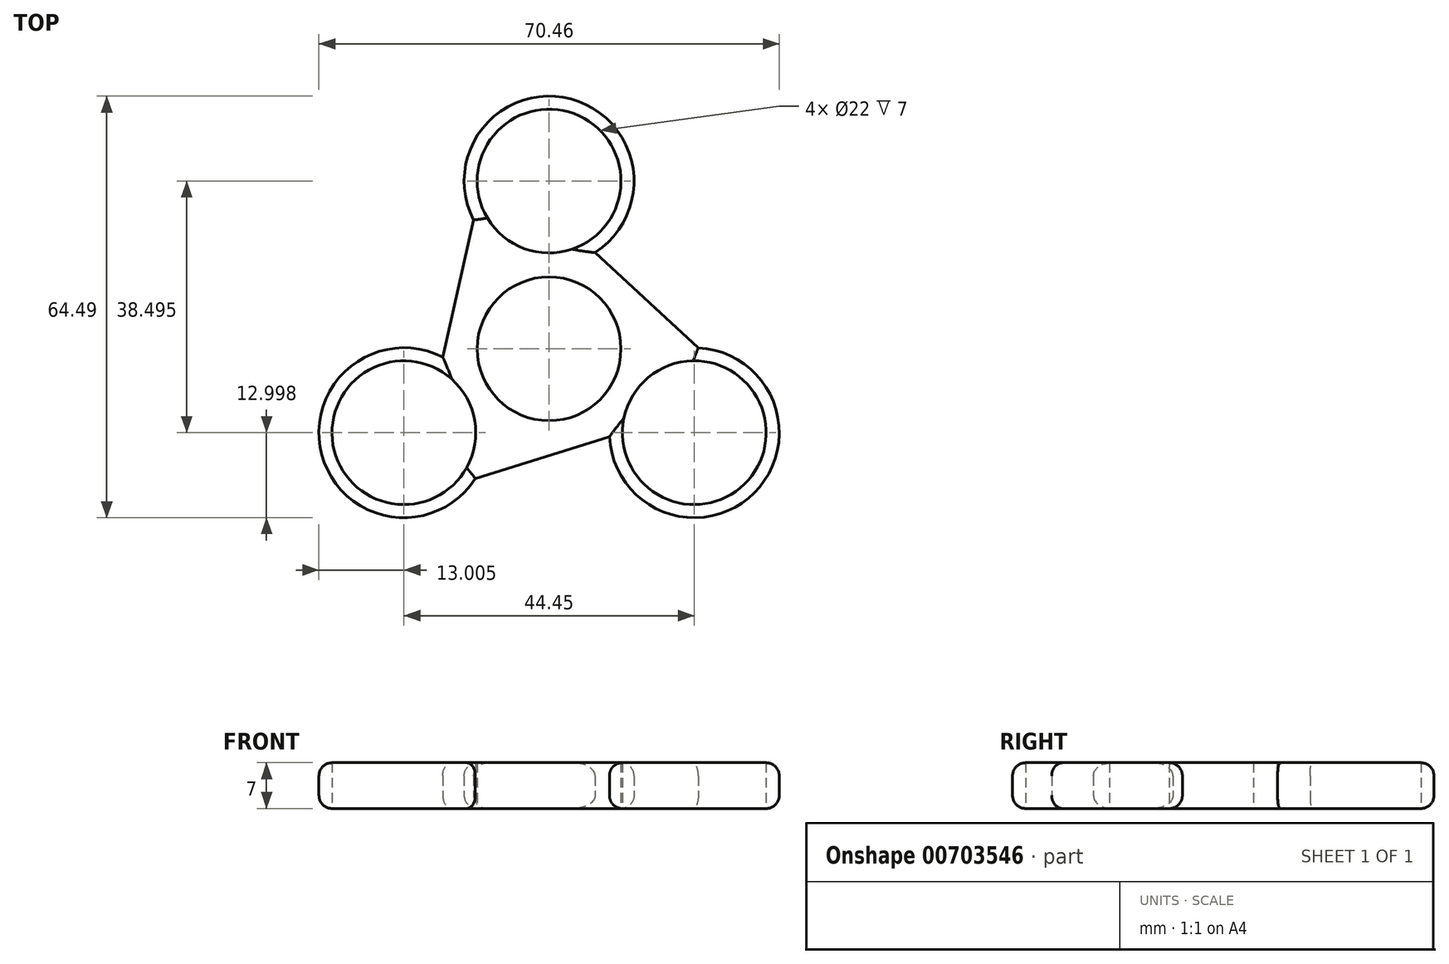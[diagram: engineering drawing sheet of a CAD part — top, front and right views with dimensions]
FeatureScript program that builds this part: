
annotation { "Feature Type Name" : "Feature", "Feature Type Description" : "" }
export const myFeature = defineFeature(function(context is Context, id is Id, definition is map)
    precondition{}
    {
        {
            var Q0;
            Q0=qCreatedBy(makeId("Top.planeOp"),FACE);
            var sketch = newSketch(context, id + "F0", { "sketchPlane" : qUnion([Q0])});
            skCircle(sketch, "E0", {"center": v(0, 0) * mm, "radius": 11 * mm});
            skCircle(sketch, "E1", {"center": v(0, 0) * mm, "radius": 25.66 * mm});
            skLineSegment(sketch, "E2", {"start": v(0, 0) * mm, "end": v(0, 25.66) * mm});
            skLineSegment(sketch, "E3", {"start": v(0, 0) * mm, "end": v(-22.23, -12.83) * mm});
            skLineSegment(sketch, "E4", {"start": v(0, 0) * mm, "end": v(22.22, -12.83) * mm});
            skLineSegment(sketch, "E5", {"start": v(-22.23, -12.83) * mm, "end": v(22.22, -12.83) * mm});
            skLineSegment(sketch, "E6", {"start": v(0, 25.66) * mm, "end": v(22.22, -12.83) * mm});
            skLineSegment(sketch, "E7", {"start": v(0, 25.66) * mm, "end": v(-22.23, -12.83) * mm});
            skCircle(sketch, "E8", {"center": v(0, 25.66) * mm, "radius": 11 * mm});
            skCircle(sketch, "E9", {"center": v(22.22, -12.83) * mm, "radius": 11 * mm});
            skCircle(sketch, "E10", {"center": v(-22.23, -12.83) * mm, "radius": 11 * mm});
            skLineSegment(sketch, "E11", {"start": v(-10.74, 23.3) * mm, "end": v(-16.73, -3.3) * mm});
            skLineSegment(sketch, "E12", {"start": v(10.74, 23.3) * mm, "end": v(0, 0) * mm});
            skLineSegment(sketch, "E13", {"start": v(-25.56, -2.35) * mm, "end": v(0, 0) * mm});
            skLineSegment(sketch, "E14", {"start": v(14.81, -20.96) * mm, "end": v(0, 0) * mm});
            skCircle(sketch, "E15", {"center": v(-22.23, -12.83) * mm, "radius": 13 * mm});
            skCircle(sketch, "E16", {"center": v(22.22, -12.83) * mm, "radius": 13 * mm});
            skCircle(sketch, "E17", {"center": v(0, 25.66) * mm, "radius": 13 * mm});
            skLineSegment(sketch, "E18", {"start": v(-72.04, -0.14) * mm, "end": v(-63.63, 27.97) * mm});
            skLineSegment(sketch, "E19", {"start": v(25.56, -2.35) * mm, "end": v(5.5, 16.14) * mm});
            skLineSegment(sketch, "E20", {"start": v(-14.81, -20.96) * mm, "end": v(11.22, -12.83) * mm});
            skSolve(sketch);
        }
        {
            var Q0;
            {var subQ1=sQuery(id+"F0.wireOp",EDGE,"E0");var subQ7=sQuery(id+"F0.wireOp",EDGE,"E2");var subQ8=makeQuery(id+"F0.imprint","INTERSECT",VERTEX,{"derivedFrom":[subQ1,subQ7]});Q0=makeQuery(id+"F0.imprint","IMPRINT",FACE,{"disambiguationData":[TD([[makeQuery(id+"F0.imprint","IMPRINT",EDGE,{"disambiguationData":[TD([[subQ8,-1.0]])],"derivedFrom":subQ1}),-1.0]])]});}
            var Q1;
            {var subQ0=sQuery(id+"F0.wireOp",EDGE,"E12");var subQ1=sQuery(id+"F0.wireOp",EDGE,"E0");var subQ2=makeQuery(id+"F0.imprint","INTERSECT",VERTEX,{"derivedFrom":[subQ1,subQ0]});Q1=makeQuery(id+"F0.imprint","IMPRINT",FACE,{"disambiguationData":[TD([[makeQuery(id+"F0.imprint","IMPRINT",EDGE,{"disambiguationData":[TD([[subQ2,1.0]])],"derivedFrom":subQ1}),-1.0]])]});}
            var Q2;
            {var subQ1=sQuery(id+"F0.wireOp",EDGE,"E0");var subQ7=sQuery(id+"F0.wireOp",EDGE,"E3");var subQ8=makeQuery(id+"F0.imprint","INTERSECT",VERTEX,{"derivedFrom":[subQ1,subQ7]});Q2=makeQuery(id+"F0.imprint","IMPRINT",FACE,{"disambiguationData":[TD([[makeQuery(id+"F0.imprint","IMPRINT",EDGE,{"disambiguationData":[TD([[subQ8,-1.0]])],"derivedFrom":subQ1}),-1.0]])]});}
            var Q3;
            {var subQ0=sQuery(id+"F0.wireOp",EDGE,"E13");var subQ1=sQuery(id+"F0.wireOp",EDGE,"E0");var subQ2=makeQuery(id+"F0.imprint","INTERSECT",VERTEX,{"derivedFrom":[subQ1,subQ0]});Q3=makeQuery(id+"F0.imprint","IMPRINT",FACE,{"disambiguationData":[TD([[makeQuery(id+"F0.imprint","IMPRINT",EDGE,{"disambiguationData":[TD([[subQ2,-1.0]])],"derivedFrom":subQ1}),-1.0]])]});}
            var Q4;
            {var subQ5=sQuery(id+"F0.wireOp",EDGE,"E0");var subQ7=sQuery(id+"F0.wireOp",EDGE,"E2");var subQ8=makeQuery(id+"F0.imprint","INTERSECT",VERTEX,{"derivedFrom":[subQ5,subQ7]});Q4=makeQuery(id+"F0.imprint","IMPRINT",FACE,{"disambiguationData":[TD([[makeQuery(id+"F0.imprint","IMPRINT",EDGE,{"disambiguationData":[TD([[subQ8,1.0]])],"derivedFrom":subQ5}),-1.0]])]});}
            var Q5;
            {var subQ0=sQuery(id+"F0.wireOp",EDGE,"E14");var subQ7=sQuery(id+"F0.wireOp",EDGE,"E0");var subQ9=makeQuery(id+"F0.imprint","INTERSECT",VERTEX,{"derivedFrom":[subQ7,subQ0]});Q5=makeQuery(id+"F0.imprint","IMPRINT",FACE,{"disambiguationData":[TD([[makeQuery(id+"F0.imprint","IMPRINT",EDGE,{"disambiguationData":[TD([[subQ9,-1.0]])],"derivedFrom":subQ7}),-1.0]])]});}
            var Q6;
            {var subQ5=sQuery(id+"F0.wireOp",EDGE,"E15");var subQ6=sQuery(id+"F0.wireOp",EDGE,"E5");var subQ7=makeQuery(id+"F0.imprint","INTERSECT",VERTEX,{"derivedFrom":[subQ6,subQ5]});Q6=makeQuery(id+"F0.imprint","IMPRINT",FACE,{"disambiguationData":[TD([[makeQuery(id+"F0.imprint","IMPRINT",EDGE,{"disambiguationData":[TD([[subQ7,-1.0]])],"derivedFrom":subQ6}),-1.0]])]});}
            var Q7;
            {var subQ1=sQuery(id+"F0.wireOp",EDGE,"E6");var subQ5=sQuery(id+"F0.wireOp",EDGE,"E12");var subQ6=makeQuery(id+"F0.imprint","INTERSECT",VERTEX,{"derivedFrom":[subQ1,subQ5]});Q7=makeQuery(id+"F0.imprint","IMPRINT",FACE,{"disambiguationData":[TD([[makeQuery(id+"F0.imprint","IMPRINT",EDGE,{"disambiguationData":[TD([[subQ6,-1.0]])],"derivedFrom":subQ1}),1.0]])]});}
            var Q8;
            {var subQ5=sQuery(id+"F0.wireOp",EDGE,"E17");var subQ7=sQuery(id+"F0.wireOp",EDGE,"E7");var subQ9=makeQuery(id+"F0.imprint","INTERSECT",VERTEX,{"derivedFrom":[subQ7,subQ5]});Q8=makeQuery(id+"F0.imprint","IMPRINT",FACE,{"disambiguationData":[TD([[makeQuery(id+"F0.imprint","IMPRINT",EDGE,{"disambiguationData":[TD([[subQ9,-1.0]])],"derivedFrom":subQ7}),-1.0]])]});}
            var Q9;
            {var subQ0=sQuery(id+"F0.wireOp",EDGE,"E8");var subQ1=sQuery(id+"F0.wireOp",EDGE,"E7");var subQ2=makeQuery(id+"F0.imprint","INTERSECT",VERTEX,{"derivedFrom":[subQ1,subQ0]});Q9=makeQuery(id+"F0.imprint","IMPRINT",FACE,{"disambiguationData":[TD([[makeQuery(id+"F0.imprint","IMPRINT",EDGE,{"disambiguationData":[TD([[subQ2,-1.0]])],"derivedFrom":subQ1}),-1.0]])]});}
            var Q10;
            {var subQ1=sQuery(id+"F0.wireOp",EDGE,"E1");var subQ3=sQuery(id+"F0.wireOp",EDGE,"E17");var subQ4=makeQuery(id+"F0.imprint","INTERSECT",VERTEX,{"disambiguationData":[OD(1.0)],"derivedFrom":[subQ1,subQ3]});Q10=makeQuery(id+"F0.imprint","IMPRINT",FACE,{"disambiguationData":[TD([[makeQuery(id+"F0.imprint","IMPRINT",EDGE,{"disambiguationData":[TD([[subQ4,-1.0]])],"derivedFrom":subQ3}),1.0]])]});}
            var Q11;
            {var subQ1=sQuery(id+"F0.wireOp",EDGE,"E1");var subQ3=sQuery(id+"F0.wireOp",EDGE,"E17");var subQ4=makeQuery(id+"F0.imprint","INTERSECT",VERTEX,{"disambiguationData":[OD(0.0)],"derivedFrom":[subQ1,subQ3]});Q11=makeQuery(id+"F0.imprint","IMPRINT",FACE,{"disambiguationData":[TD([[makeQuery(id+"F0.imprint","IMPRINT",EDGE,{"disambiguationData":[TD([[subQ4,-1.0]])],"derivedFrom":subQ3}),1.0]])]});}
            var Q12;
            {var subQ0=sQuery(id+"F0.wireOp",EDGE,"E16");var subQ1=sQuery(id+"F0.wireOp",EDGE,"E6");var subQ2=makeQuery(id+"F0.imprint","INTERSECT",VERTEX,{"derivedFrom":[subQ1,subQ0]});Q12=makeQuery(id+"F0.imprint","IMPRINT",FACE,{"disambiguationData":[TD([[makeQuery(id+"F0.imprint","IMPRINT",EDGE,{"disambiguationData":[TD([[subQ2,-1.0]])],"derivedFrom":subQ1}),1.0]])]});}
            var Q13;
            {var subQ1=sQuery(id+"F0.wireOp",EDGE,"E1");var subQ3=sQuery(id+"F0.wireOp",EDGE,"E16");var subQ4=makeQuery(id+"F0.imprint","INTERSECT",VERTEX,{"disambiguationData":[OD(1.0)],"derivedFrom":[subQ1,subQ3]});Q13=makeQuery(id+"F0.imprint","IMPRINT",FACE,{"disambiguationData":[TD([[makeQuery(id+"F0.imprint","IMPRINT",EDGE,{"disambiguationData":[TD([[subQ4,-1.0]])],"derivedFrom":subQ3}),1.0]])]});}
            var Q14;
            {var subQ1=sQuery(id+"F0.wireOp",EDGE,"E1");var subQ3=sQuery(id+"F0.wireOp",EDGE,"E16");var subQ4=makeQuery(id+"F0.imprint","INTERSECT",VERTEX,{"disambiguationData":[OD(0.0)],"derivedFrom":[subQ1,subQ3]});Q14=makeQuery(id+"F0.imprint","IMPRINT",FACE,{"disambiguationData":[TD([[makeQuery(id+"F0.imprint","IMPRINT",EDGE,{"disambiguationData":[TD([[subQ4,-1.0]])],"derivedFrom":subQ3}),1.0]])]});}
            var Q15;
            {var subQ0=sQuery(id+"F0.wireOp",EDGE,"E16");var subQ1=sQuery(id+"F0.wireOp",EDGE,"E4");var subQ2=makeQuery(id+"F0.imprint","INTERSECT",VERTEX,{"derivedFrom":[subQ1,subQ0]});Q15=makeQuery(id+"F0.imprint","IMPRINT",FACE,{"disambiguationData":[TD([[makeQuery(id+"F0.imprint","IMPRINT",EDGE,{"disambiguationData":[TD([[subQ2,-1.0]])],"derivedFrom":subQ1}),1.0]])]});}
            var Q16;
            {var subQ0=sQuery(id+"F0.wireOp",EDGE,"E16");var subQ1=sQuery(id+"F0.wireOp",EDGE,"E4");var subQ2=makeQuery(id+"F0.imprint","INTERSECT",VERTEX,{"derivedFrom":[subQ1,subQ0]});Q16=makeQuery(id+"F0.imprint","IMPRINT",FACE,{"disambiguationData":[TD([[makeQuery(id+"F0.imprint","IMPRINT",EDGE,{"disambiguationData":[TD([[subQ2,-1.0]])],"derivedFrom":subQ1}),-1.0]])]});}
            var Q17;
            {var subQ0=sQuery(id+"F0.wireOp",EDGE,"E15");var subQ1=sQuery(id+"F0.wireOp",EDGE,"E3");var subQ2=makeQuery(id+"F0.imprint","INTERSECT",VERTEX,{"derivedFrom":[subQ1,subQ0]});Q17=makeQuery(id+"F0.imprint","IMPRINT",FACE,{"disambiguationData":[TD([[makeQuery(id+"F0.imprint","IMPRINT",EDGE,{"disambiguationData":[TD([[subQ2,-1.0]])],"derivedFrom":subQ1}),1.0]])]});}
            var Q18;
            {var subQ0=sQuery(id+"F0.wireOp",EDGE,"E15");var subQ1=sQuery(id+"F0.wireOp",EDGE,"E3");var subQ2=makeQuery(id+"F0.imprint","INTERSECT",VERTEX,{"derivedFrom":[subQ1,subQ0]});Q18=makeQuery(id+"F0.imprint","IMPRINT",FACE,{"disambiguationData":[TD([[makeQuery(id+"F0.imprint","IMPRINT",EDGE,{"disambiguationData":[TD([[subQ2,-1.0]])],"derivedFrom":subQ1}),-1.0]])]});}
            var Q19;
            {var subQ0=sQuery(id+"F0.wireOp",EDGE,"E17");var subQ1=sQuery(id+"F0.wireOp",EDGE,"E2");var subQ2=makeQuery(id+"F0.imprint","INTERSECT",VERTEX,{"derivedFrom":[subQ1,subQ0]});Q19=makeQuery(id+"F0.imprint","IMPRINT",FACE,{"disambiguationData":[TD([[makeQuery(id+"F0.imprint","IMPRINT",EDGE,{"disambiguationData":[TD([[subQ2,-1.0]])],"derivedFrom":subQ1}),1.0]])]});}
            var Q20;
            {var subQ0=sQuery(id+"F0.wireOp",EDGE,"E17");var subQ1=sQuery(id+"F0.wireOp",EDGE,"E2");var subQ2=makeQuery(id+"F0.imprint","INTERSECT",VERTEX,{"derivedFrom":[subQ1,subQ0]});Q20=makeQuery(id+"F0.imprint","IMPRINT",FACE,{"disambiguationData":[TD([[makeQuery(id+"F0.imprint","IMPRINT",EDGE,{"disambiguationData":[TD([[subQ2,-1.0]])],"derivedFrom":subQ1}),-1.0]])]});}
            extrude(context, id + "F1", {"entities" : qUnion([Q0, Q1, Q2, Q3, Q4, Q5, Q6, Q7, Q8, Q9, Q10, Q11, Q12, Q13, Q14, Q15, Q16, Q17, Q18, Q19, Q20]), "depth" : 7 * mm, "offsetDistance" : 25.4 * mm});
        }
        {
            var Q0;
            {var subQ0=sQuery(id+"F0.wireOp",EDGE,"E10");var subQ1=sQuery(id+"F0.wireOp",EDGE,"E5");var subQ2=makeQuery(id+"F0.imprint","INTERSECT",VERTEX,{"derivedFrom":[subQ1,subQ0]});Q0=makeQuery(id+"F0.imprint","IMPRINT",FACE,{"disambiguationData":[TD([[makeQuery(id+"F0.imprint","IMPRINT",EDGE,{"disambiguationData":[TD([[subQ2,-1.0]])],"derivedFrom":subQ1}),-1.0]])]});}
            var Q1;
            {var subQ1=sQuery(id+"F0.wireOp",EDGE,"E1");var subQ3=sQuery(id+"F0.wireOp",EDGE,"E15");var subQ4=makeQuery(id+"F0.imprint","INTERSECT",VERTEX,{"disambiguationData":[OD(1.0)],"derivedFrom":[subQ1,subQ3]});Q1=makeQuery(id+"F0.imprint","IMPRINT",FACE,{"disambiguationData":[TD([[makeQuery(id+"F0.imprint","IMPRINT",EDGE,{"disambiguationData":[TD([[subQ4,-1.0]])],"derivedFrom":subQ3}),1.0]])]});}
            var Q2;
            {var subQ1=sQuery(id+"F0.wireOp",EDGE,"E9");var subQ3=sQuery(id+"F0.wireOp",EDGE,"E14");var subQ4=makeQuery(id+"F0.imprint","INTERSECT",VERTEX,{"derivedFrom":[subQ1,subQ3]});Q2=makeQuery(id+"F0.imprint","IMPRINT",FACE,{"disambiguationData":[TD([[makeQuery(id+"F0.imprint","IMPRINT",EDGE,{"disambiguationData":[TD([[subQ4,-1.0]])],"derivedFrom":subQ3}),-1.0]])]});}
            extrude(context, id + "F2", {"entities" : qUnion([Q0, Q1, Q2]), "operationType" : NewBodyOperationType.ADD, "depth" : 7 * mm, "offsetDistance" : 25.4 * mm});
        }
        {
            var Q0;
            {var subQ1=sQuery(id+"F0.wireOp",EDGE,"E8");var subQ3=sQuery(id+"F0.wireOp",EDGE,"E12");var subQ4=makeQuery(id+"F0.imprint","INTERSECT",VERTEX,{"derivedFrom":[subQ1,subQ3]});Q0=makeQuery(id+"F0.imprint","IMPRINT",FACE,{"disambiguationData":[TD([[makeQuery(id+"F0.imprint","IMPRINT",EDGE,{"disambiguationData":[TD([[subQ4,-1.0]])],"derivedFrom":subQ3}),-1.0]])]});}
            var Q1;
            {var subQ0=sQuery(id+"F0.wireOp",EDGE,"E20");var subQ5=sQuery(id+"F0.wireOp",EDGE,"E14");var subQ6=makeQuery(id+"F0.imprint","INTERSECT",VERTEX,{"derivedFrom":[subQ5,subQ0]});Q1=makeQuery(id+"F0.imprint","IMPRINT",FACE,{"disambiguationData":[TD([[makeQuery(id+"F0.imprint","IMPRINT",EDGE,{"disambiguationData":[TD([[subQ6,-1.0]])],"derivedFrom":subQ5}),-1.0]])]});}
            var Q2;
            {var subQ0=sQuery(id+"F0.wireOp",EDGE,"E14");var subQ1=sQuery(id+"F0.wireOp",EDGE,"E5");var subQ2=makeQuery(id+"F0.imprint","INTERSECT",VERTEX,{"derivedFrom":[subQ1,subQ0]});Q2=makeQuery(id+"F0.imprint","IMPRINT",FACE,{"disambiguationData":[TD([[makeQuery(id+"F0.imprint","IMPRINT",EDGE,{"disambiguationData":[TD([[subQ2,-1.0]])],"derivedFrom":subQ1}),-1.0]])]});}
            var Q3;
            {var subQ0=sQuery(id+"F0.wireOp",EDGE,"E20");var subQ1=sQuery(id+"F0.wireOp",EDGE,"E14");var subQ2=makeQuery(id+"F0.imprint","INTERSECT",VERTEX,{"derivedFrom":[subQ1,subQ0]});Q3=makeQuery(id+"F0.imprint","IMPRINT",FACE,{"disambiguationData":[TD([[makeQuery(id+"F0.imprint","IMPRINT",EDGE,{"disambiguationData":[TD([[subQ2,-1.0]])],"derivedFrom":subQ1}),1.0]])]});}
            var Q4;
            {var subQ5=sQuery(id+"F0.wireOp",EDGE,"E14");var subQ6=sQuery(id+"F0.wireOp",EDGE,"E9");var subQ8=makeQuery(id+"F0.imprint","INTERSECT",VERTEX,{"derivedFrom":[subQ6,subQ5]});Q4=makeQuery(id+"F0.imprint","IMPRINT",FACE,{"disambiguationData":[TD([[makeQuery(id+"F0.imprint","IMPRINT",EDGE,{"disambiguationData":[TD([[subQ8,-1.0]])],"derivedFrom":subQ5}),1.0]])]});}
            var Q5;
            {var subQ0=sQuery(id+"F0.wireOp",EDGE,"E15");var subQ1=sQuery(id+"F0.wireOp",EDGE,"E11");var subQ2=makeQuery(id+"F0.imprint","INTERSECT",VERTEX,{"derivedFrom":[subQ1,subQ0]});Q5=makeQuery(id+"F0.imprint","IMPRINT",FACE,{"disambiguationData":[TD([[makeQuery(id+"F0.imprint","IMPRINT",EDGE,{"disambiguationData":[TD([[subQ2,-1.0]])],"derivedFrom":subQ1}),1.0]])]});}
            var Q6;
            {var subQ0=sQuery(id+"F0.wireOp",EDGE,"E11");var subQ5=sQuery(id+"F0.wireOp",EDGE,"E13");var subQ6=makeQuery(id+"F0.imprint","INTERSECT",VERTEX,{"derivedFrom":[subQ0,subQ5]});Q6=makeQuery(id+"F0.imprint","IMPRINT",FACE,{"disambiguationData":[TD([[makeQuery(id+"F0.imprint","IMPRINT",EDGE,{"disambiguationData":[TD([[subQ6,-1.0]])],"derivedFrom":subQ5}),-1.0]])]});}
            var Q7;
            {var subQ0=sQuery(id+"F0.wireOp",EDGE,"E13");var subQ1=sQuery(id+"F0.wireOp",EDGE,"E7");var subQ2=makeQuery(id+"F0.imprint","INTERSECT",VERTEX,{"derivedFrom":[subQ1,subQ0]});Q7=makeQuery(id+"F0.imprint","IMPRINT",FACE,{"disambiguationData":[TD([[makeQuery(id+"F0.imprint","IMPRINT",EDGE,{"disambiguationData":[TD([[subQ2,-1.0]])],"derivedFrom":subQ1}),-1.0]])]});}
            var Q8;
            {var subQ0=sQuery(id+"F0.wireOp",EDGE,"E19");var subQ5=sQuery(id+"F0.wireOp",EDGE,"E12");var subQ6=makeQuery(id+"F0.imprint","INTERSECT",VERTEX,{"derivedFrom":[subQ5,subQ0]});Q8=makeQuery(id+"F0.imprint","IMPRINT",FACE,{"disambiguationData":[TD([[makeQuery(id+"F0.imprint","IMPRINT",EDGE,{"disambiguationData":[TD([[subQ6,-1.0]])],"derivedFrom":subQ5}),-1.0]])]});}
            var Q9;
            {var subQ0=sQuery(id+"F0.wireOp",EDGE,"E17");var subQ1=sQuery(id+"F0.wireOp",EDGE,"E6");var subQ2=makeQuery(id+"F0.imprint","INTERSECT",VERTEX,{"derivedFrom":[subQ1,subQ0]});Q9=makeQuery(id+"F0.imprint","IMPRINT",FACE,{"disambiguationData":[TD([[makeQuery(id+"F0.imprint","IMPRINT",EDGE,{"disambiguationData":[TD([[subQ2,-1.0]])],"derivedFrom":subQ1}),1.0]])]});}
            var Q10;
            {var subQ0=sQuery(id+"F0.wireOp",EDGE,"E19");var subQ1=sQuery(id+"F0.wireOp",EDGE,"E12");var subQ2=makeQuery(id+"F0.imprint","INTERSECT",VERTEX,{"derivedFrom":[subQ1,subQ0]});Q10=makeQuery(id+"F0.imprint","IMPRINT",FACE,{"disambiguationData":[TD([[makeQuery(id+"F0.imprint","IMPRINT",EDGE,{"disambiguationData":[TD([[subQ2,-1.0]])],"derivedFrom":subQ1}),1.0]])]});}
            var Q11;
            {var subQ5=sQuery(id+"F0.wireOp",EDGE,"E12");var subQ6=sQuery(id+"F0.wireOp",EDGE,"E8");var subQ7=makeQuery(id+"F0.imprint","INTERSECT",VERTEX,{"derivedFrom":[subQ6,subQ5]});Q11=makeQuery(id+"F0.imprint","IMPRINT",FACE,{"disambiguationData":[TD([[makeQuery(id+"F0.imprint","IMPRINT",EDGE,{"disambiguationData":[TD([[subQ7,-1.0]])],"derivedFrom":subQ5}),1.0]])]});}
            extrude(context, id + "F3", {"entities" : qUnion([Q0, Q1, Q2, Q3, Q4, Q5, Q6, Q7, Q8, Q9, Q10, Q11]), "operationType" : NewBodyOperationType.ADD, "depth" : 7 * mm, "offsetDistance" : 25.4 * mm});
        }
        {
            var Q0;
            {var subQ3=sQuery(id+"F0.wireOp",EDGE,"E11");var subQ5=sQuery(id+"F0.wireOp",EDGE,"E15");var subQ6=makeQuery(id+"F0.imprint","INTERSECT",VERTEX,{"derivedFrom":[subQ3,subQ5]});Q0=makeQuery(id+"F0.imprint","IMPRINT",FACE,{"disambiguationData":[TD([[makeQuery(id+"F0.imprint","IMPRINT",EDGE,{"disambiguationData":[TD([[subQ6,-1.0]])],"derivedFrom":subQ3}),-1.0]])]});}
            var Q1;
            {var subQ1=sQuery(id+"F0.wireOp",EDGE,"E10");var subQ3=sQuery(id+"F0.wireOp",EDGE,"E13");var subQ4=makeQuery(id+"F0.imprint","INTERSECT",VERTEX,{"derivedFrom":[subQ1,subQ3]});Q1=makeQuery(id+"F0.imprint","IMPRINT",FACE,{"disambiguationData":[TD([[makeQuery(id+"F0.imprint","IMPRINT",EDGE,{"disambiguationData":[TD([[subQ4,-1.0]])],"derivedFrom":subQ3}),-1.0]])]});}
            var Q2;
            {var subQ1=sQuery(id+"F0.wireOp",EDGE,"E1");var subQ3=sQuery(id+"F0.wireOp",EDGE,"E15");var subQ4=makeQuery(id+"F0.imprint","INTERSECT",VERTEX,{"disambiguationData":[OD(0.0)],"derivedFrom":[subQ1,subQ3]});Q2=makeQuery(id+"F0.imprint","IMPRINT",FACE,{"disambiguationData":[TD([[makeQuery(id+"F0.imprint","IMPRINT",EDGE,{"disambiguationData":[TD([[subQ4,-1.0]])],"derivedFrom":subQ3}),1.0]])]});}
            extrude(context, id + "F4", {"entities" : qUnion([Q0, Q1, Q2]), "operationType" : NewBodyOperationType.ADD, "depth" : 7 * mm, "offsetDistance" : 25.4 * mm});
        }
        {
            var Q0;
            Q0=makeQuery(id+"F1.opExtrude","CAP_EDGE",EDGE,{"disambiguationData":[OSD([sQuery(id+"F0.wireOp",EDGE,"E19")])],"isStart":false});
            var Q1;
            {var subQ0=sQuery(id+"F0.wireOp",EDGE,"E11");Q1=makeQuery(id+"F3.boolean.opBoolean","MERGE",EDGE,{"derivedFrom":[makeQuery(id+"F1.opExtrude","CAP_EDGE",EDGE,{"disambiguationData":[OSD([subQ0])],"isStart":false}),makeQuery(id+"F3.opExtrude","CAP_EDGE",EDGE,{"disambiguationData":[OSD([subQ0])],"isStart":false})]});}
            var Q2;
            Q2=makeQuery(id+"F1.opExtrude","CAP_EDGE",EDGE,{"disambiguationData":[OSD([sQuery(id+"F0.wireOp",EDGE,"E20")])],"isStart":false});
            var Q3;
            {var subQ0=sQuery(id+"F0.wireOp",EDGE,"E15");Q3=makeQuery(id+"F4.boolean.opBoolean","MERGE",EDGE,{"derivedFrom":[makeQuery(id+"F2.opExtrude","CAP_EDGE",EDGE,{"disambiguationData":[OSD([subQ0])],"isStart":false}),makeQuery(id+"F4.opExtrude","CAP_EDGE",EDGE,{"disambiguationData":[OSD([subQ0])],"isStart":false})]});}
            var Q4;
            {var subQ0=sQuery(id+"F0.wireOp",EDGE,"E16");var subQ1=sQuery(id+"F0.wireOp",EDGE,"E1");var subQ2=makeQuery(id+"F0.imprint","INTERSECT",VERTEX,{"disambiguationData":[OD(1.0)],"derivedFrom":[subQ1,subQ0]});Q4=makeQuery(id+"F3.boolean.opBoolean","MERGE",EDGE,{"derivedFrom":[makeQuery(id+"F1.opExtrude","CAP_EDGE",EDGE,{"disambiguationData":[OSD([subQ0]),TDD([makeQuery(id+"F0.imprint","IMPRINT",EDGE,{"disambiguationData":[TD([[subQ2,-1.0]])],"derivedFrom":subQ0}),makeQuery(id+"F0.imprint","IMPRINT",EDGE,{"disambiguationData":[TD([[makeQuery(id+"F0.imprint","INTERSECT",VERTEX,{"disambiguationData":[OD(0.0)],"derivedFrom":[subQ1,subQ0]}),-1.0]])],"derivedFrom":subQ0})])],"isStart":false}),makeQuery(id+"F3.opExtrude","CAP_EDGE",EDGE,{"disambiguationData":[OSD([subQ0])],"isStart":false})]});}
            var Q5;
            {var subQ0=sQuery(id+"F0.wireOp",EDGE,"E17");var subQ1=sQuery(id+"F0.wireOp",EDGE,"E1");var subQ2=makeQuery(id+"F0.imprint","INTERSECT",VERTEX,{"disambiguationData":[OD(1.0)],"derivedFrom":[subQ1,subQ0]});Q5=makeQuery(id+"F3.boolean.opBoolean","MERGE",EDGE,{"derivedFrom":[makeQuery(id+"F1.opExtrude","CAP_EDGE",EDGE,{"disambiguationData":[OSD([subQ0]),TDD([makeQuery(id+"F0.imprint","IMPRINT",EDGE,{"disambiguationData":[TD([[subQ2,-1.0]])],"derivedFrom":subQ0}),makeQuery(id+"F0.imprint","IMPRINT",EDGE,{"disambiguationData":[TD([[makeQuery(id+"F0.imprint","INTERSECT",VERTEX,{"disambiguationData":[OD(0.0)],"derivedFrom":[subQ1,subQ0]}),-1.0]])],"derivedFrom":subQ0})])],"isStart":false}),makeQuery(id+"F3.opExtrude","CAP_EDGE",EDGE,{"disambiguationData":[OSD([subQ0])],"isStart":false})]});}
            var Q6;
            Q6=makeQuery(id+"F1.opExtrude","CAP_EDGE",EDGE,{"disambiguationData":[OSD([sQuery(id+"F0.wireOp",EDGE,"E20")])],"isStart":true});
            var Q7;
            Q7=makeQuery(id+"F1.opExtrude","CAP_EDGE",EDGE,{"disambiguationData":[OSD([sQuery(id+"F0.wireOp",EDGE,"E19")])],"isStart":true});
            var Q8;
            {var subQ0=sQuery(id+"F0.wireOp",EDGE,"E11");Q8=makeQuery(id+"F3.boolean.opBoolean","MERGE",EDGE,{"derivedFrom":[makeQuery(id+"F1.opExtrude","CAP_EDGE",EDGE,{"disambiguationData":[OSD([subQ0])],"isStart":true}),makeQuery(id+"F3.opExtrude","CAP_EDGE",EDGE,{"disambiguationData":[OSD([subQ0])],"isStart":true})]});}
            var Q9;
            {var subQ0=sQuery(id+"F0.wireOp",EDGE,"E15");Q9=makeQuery(id+"F4.boolean.opBoolean","MERGE",EDGE,{"derivedFrom":[makeQuery(id+"F2.opExtrude","CAP_EDGE",EDGE,{"disambiguationData":[OSD([subQ0])],"isStart":true}),makeQuery(id+"F4.opExtrude","CAP_EDGE",EDGE,{"disambiguationData":[OSD([subQ0])],"isStart":true})]});}
            var Q10;
            {var subQ0=sQuery(id+"F0.wireOp",EDGE,"E17");var subQ1=sQuery(id+"F0.wireOp",EDGE,"E1");var subQ2=makeQuery(id+"F0.imprint","INTERSECT",VERTEX,{"disambiguationData":[OD(1.0)],"derivedFrom":[subQ1,subQ0]});Q10=makeQuery(id+"F3.boolean.opBoolean","MERGE",EDGE,{"derivedFrom":[makeQuery(id+"F1.opExtrude","CAP_EDGE",EDGE,{"disambiguationData":[OSD([subQ0]),TDD([makeQuery(id+"F0.imprint","IMPRINT",EDGE,{"disambiguationData":[TD([[subQ2,-1.0]])],"derivedFrom":subQ0}),makeQuery(id+"F0.imprint","IMPRINT",EDGE,{"disambiguationData":[TD([[makeQuery(id+"F0.imprint","INTERSECT",VERTEX,{"disambiguationData":[OD(0.0)],"derivedFrom":[subQ1,subQ0]}),-1.0]])],"derivedFrom":subQ0})])],"isStart":true}),makeQuery(id+"F3.opExtrude","CAP_EDGE",EDGE,{"disambiguationData":[OSD([subQ0])],"isStart":true})]});}
            var Q11;
            {var subQ0=sQuery(id+"F0.wireOp",EDGE,"E16");var subQ1=sQuery(id+"F0.wireOp",EDGE,"E1");var subQ2=makeQuery(id+"F0.imprint","INTERSECT",VERTEX,{"disambiguationData":[OD(1.0)],"derivedFrom":[subQ1,subQ0]});Q11=makeQuery(id+"F3.boolean.opBoolean","MERGE",EDGE,{"derivedFrom":[makeQuery(id+"F1.opExtrude","CAP_EDGE",EDGE,{"disambiguationData":[OSD([subQ0]),TDD([makeQuery(id+"F0.imprint","IMPRINT",EDGE,{"disambiguationData":[TD([[subQ2,-1.0]])],"derivedFrom":subQ0}),makeQuery(id+"F0.imprint","IMPRINT",EDGE,{"disambiguationData":[TD([[makeQuery(id+"F0.imprint","INTERSECT",VERTEX,{"disambiguationData":[OD(0.0)],"derivedFrom":[subQ1,subQ0]}),-1.0]])],"derivedFrom":subQ0})])],"isStart":true}),makeQuery(id+"F3.opExtrude","CAP_EDGE",EDGE,{"disambiguationData":[OSD([subQ0])],"isStart":true})]});}
            fillet(context, id + "F5", {"entities" : qUnion([Q0, Q1, Q2, Q3, Q4, Q5, Q6, Q7, Q8, Q9, Q10, Q11]), "radius" : 2 * mm, "tangentPropagation" : true, "allowEdgeOverflow" : false});
        }
    });
